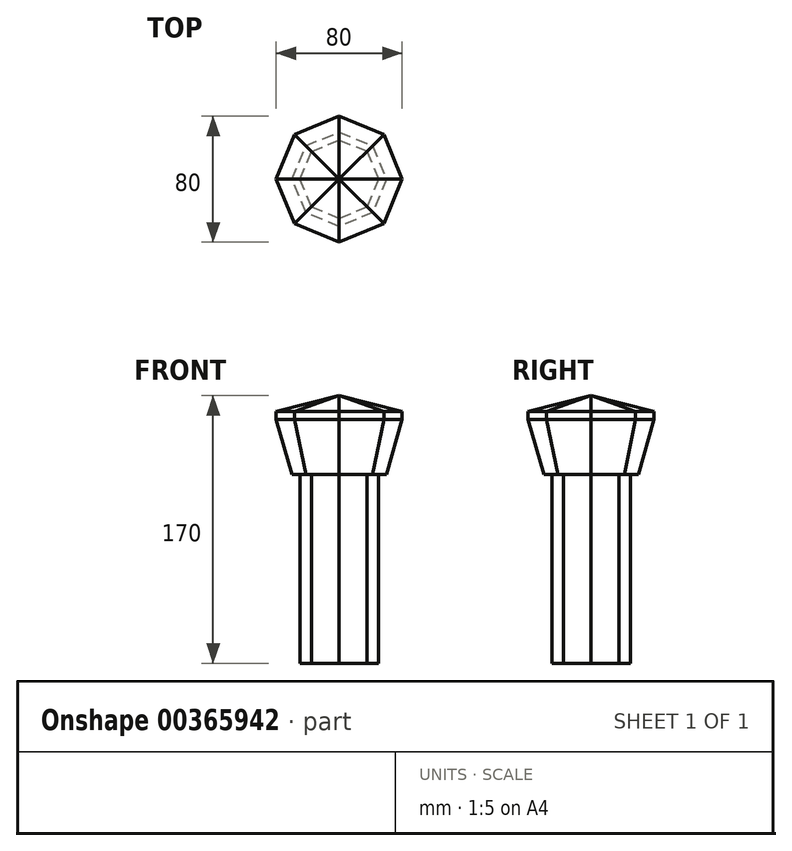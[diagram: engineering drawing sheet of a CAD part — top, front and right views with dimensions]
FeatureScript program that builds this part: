
annotation { "Feature Type Name" : "Feature", "Feature Type Description" : "" }
export const myFeature = defineFeature(function(context is Context, id is Id, definition is map)
    precondition{}
    {
        {
            var Q0;
            Q0=qCreatedBy(makeId("Front.planeOp"),FACE);
            var sketch = newSketch(context, id + "F0", { "sketchPlane" : qUnion([Q0])});
            skLineSegment(sketch, "E0", {"start": v(0, 0) * mm, "end": v(25, 0) * mm});
            skLineSegment(sketch, "E1", {"start": v(25, 0) * mm, "end": v(25, 120) * mm});
            skLineSegment(sketch, "E2", {"start": v(25, 120) * mm, "end": v(30, 120) * mm});
            skLineSegment(sketch, "E3", {"start": v(30, 120) * mm, "end": v(40, 155) * mm});
            skLineSegment(sketch, "E4", {"start": v(40, 155) * mm, "end": v(40, 160) * mm});
            skLineSegment(sketch, "E5", {"start": v(40, 160) * mm, "end": v(0, 170) * mm});
            skLineSegment(sketch, "E6", {"start": v(0, 170) * mm, "end": v(0, 0) * mm});
            skSolve(sketch);
        }
        {
            var Q0;
            Q0=qCreatedBy(makeId("Front.planeOp"),FACE);
            var Q1;
            Q1=qCreatedBy(makeId("Right.planeOp"),FACE);
            cPlane(context, id + "F1", {"entities" : qUnion([Q0, Q1]), "cplaneType" : CPlaneType.MID_PLANE, "offset" : 25 * mm, "width" : 150 * mm, "height" : 150 * mm});
        }
        {
            var Q0;
            Q0=qCreatedBy(id+"F1.planeOp",FACE);
            var sketch = newSketch(context, id + "F2", { "sketchPlane" : qUnion([Q0])});
            skLineSegment(sketch, "E7", {"start": v(0, 0) * mm, "end": v(25, 0) * mm});
            skLineSegment(sketch, "E8", {"start": v(25, 0) * mm, "end": v(25, 120) * mm});
            skLineSegment(sketch, "E9", {"start": v(25, 120) * mm, "end": v(30, 120) * mm});
            skLineSegment(sketch, "E10", {"start": v(30, 120) * mm, "end": v(40, 155) * mm});
            skLineSegment(sketch, "E11", {"start": v(40, 155) * mm, "end": v(40, 160) * mm});
            skLineSegment(sketch, "E12", {"start": v(40, 160) * mm, "end": v(0, 170) * mm});
            skLineSegment(sketch, "E13", {"start": v(0, 170) * mm, "end": v(0, 0) * mm});
            skSolve(sketch);
        }
        {
            var Q0;
            Q0=makeQuery(id+"F0.imprint","IMPRINT",FACE,{"disambiguationData":[TD([[makeQuery(id+"F0.imprint","IMPRINT",EDGE,{"derivedFrom":sQuery(id+"F0.wireOp",EDGE,"E0")}),1.0]])]});
            var Q1;
            Q1=makeQuery(id+"F2.imprint","IMPRINT",FACE,{"disambiguationData":[TD([[makeQuery(id+"F2.imprint","IMPRINT",EDGE,{"derivedFrom":sQuery(id+"F2.wireOp",EDGE,"E7")}),1.0]])]});
            var Q2;
            Q2=sQuery(id+"F0.wireOp",VERTEX,"E1.start");
            var Q3;
            Q3=sQuery(id+"F2.wireOp",VERTEX,"E8.start");
            loft(context, id + "F3", {"sheetProfilesArray" : [{ "sheetProfileEntities" : qUnion([Q0]) }, { "sheetProfileEntities" : qUnion([Q1]) }], "matchConnections" : true, "connections" : [{ "connectionEntities" : qUnion([Q2, Q3]), "connectionEdgeQueries" : qUnion([]), "connectionEdgeParameters" : [] }]});
        }
        {
            var Q0;
            Q0=makeQuery(id+"F3.opLoft","SWEPT_BODY",BODY,{"disambiguationData":[OSD([makeQuery(id+"F0.imprint","IMPRINT",FACE,{"disambiguationData":[TD([[makeQuery(id+"F0.imprint","IMPRINT",EDGE,{"derivedFrom":sQuery(id+"F0.wireOp",EDGE,"E0")}),1.0]])]}),makeQuery(id+"F2.imprint","IMPRINT",FACE,{"disambiguationData":[TD([[makeQuery(id+"F2.imprint","IMPRINT",EDGE,{"derivedFrom":sQuery(id+"F2.wireOp",EDGE,"E7")}),1.0]])]})])]});
            var Q1;
            Q1=sQuery(id+"F0.wireOp",EDGE,"E6");
            circularPattern(context, id + "F4", {"entities" : qUnion([Q0]), "axis" : qUnion([Q1]), "angle" : 360 * degree, "instanceCount" : 8, "equalSpace" : true});
        }
    });
